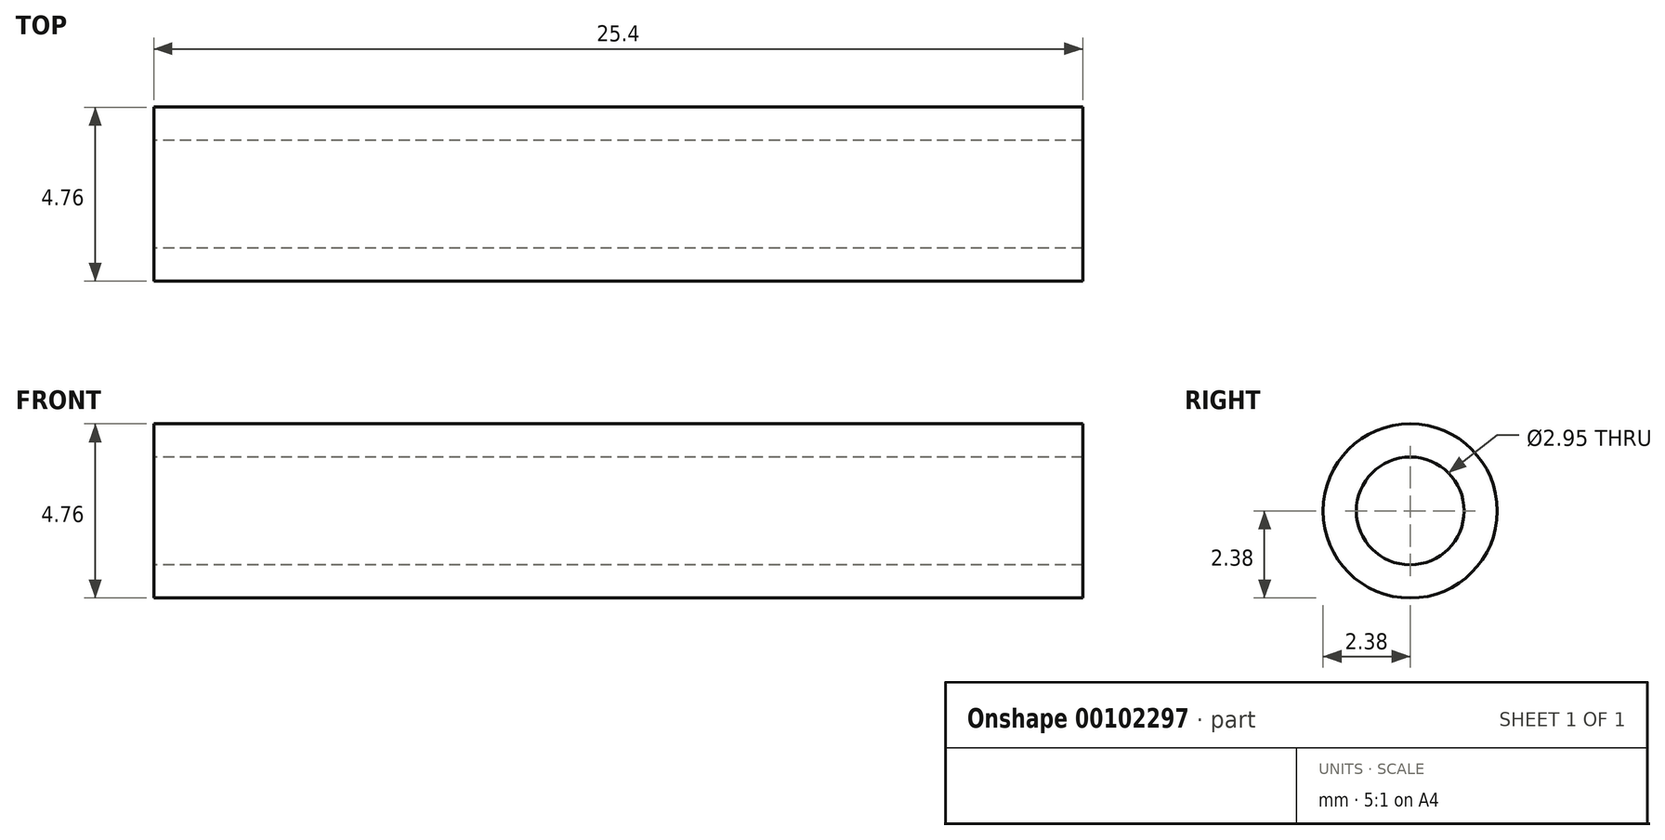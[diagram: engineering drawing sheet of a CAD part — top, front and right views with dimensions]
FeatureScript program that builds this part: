
annotation { "Feature Type Name" : "Feature", "Feature Type Description" : "" }
export const myFeature = defineFeature(function(context is Context, id is Id, definition is map)
    precondition{}
    {
        {
            var Q0;
            Q0=qCreatedBy(makeId("Right.planeOp"),FACE);
            var sketch = newSketch(context, id + "F0", { "sketchPlane" : qUnion([Q0])});
            skCircle(sketch, "E0", {"center": v(0, 0) * mm, "radius": 2.38 * mm});
            skCircle(sketch, "E1", {"center": v(0, 0) * mm, "radius": 1.47 * mm});
            skSolve(sketch);
        }
        {
            var Q0;
            Q0=qSketchRegion(id+"F0",true);
            extrude(context, id + "F1", {"entities" : qUnion([Q0]), "endBound" : BoundingType.SYMMETRIC, "depth" : 25.4 * mm});
        }
    });
